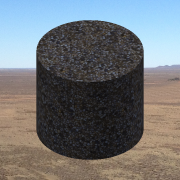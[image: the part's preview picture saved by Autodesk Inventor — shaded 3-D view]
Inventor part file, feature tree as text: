
AUTODESK INVENTOR PART (.ipt)
format: ipt  version: 2013 SP2 (Build 170200200, 200)  size: 137,728 bytes
history: native  units: in
note: dims shown in document units (in); Inventor stores cm internally (conversion verified against a paired STEP export)
features: extrude x1, sketch x1
ambient origin geometry x8: Origin, YZ Plane, XZ Plane, XY Plane, X Axis, Y Axis, Z Axis, Center Point
bodies: Solid1 (feature_tree)
feature tree (2):
  extrude  "Extrusion1"  Depth=10.0in TaperAngle=0.0deg
  sketch  "Sketch1"  dims[d0=11.25in d2=10.0in d3=0.0in]
